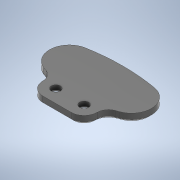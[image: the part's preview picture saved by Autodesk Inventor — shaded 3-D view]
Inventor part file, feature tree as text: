
AUTODESK INVENTOR PART (.ipt)
format: ipt  version: 2020 (Build 240168000, 168)  size: 322,048 bytes
history: native  units: mm
features: chamfer x2, extrude x1, sketch x1
ambient origin geometry x8: Origin, YZ Plane, XZ Plane, XY Plane, X Axis, Y Axis, Z Axis, Center Point
bodies: Volumenkörper1 (feature_tree)
feature tree (4):
  extrude  "Extrusion1"  Depth=70.0mm
  chamfer  "Fase1"  Distance=3.0mm
  chamfer  "Fase3"  Distance=4.0mm
  sketch  "Skizze1"  dims[d0=10.0mm d1=3.2mm d2=3.0mm d4=4.0mm d9=3.0mm d10=0.0mm d11=1.0mm d12=2.0mm d13=45.0deg d17=1.5mm d18=2.0mm d19=45.0deg d22=7.0mm d23=3.490659mm d24=22.0mm d25=70.0mm]
